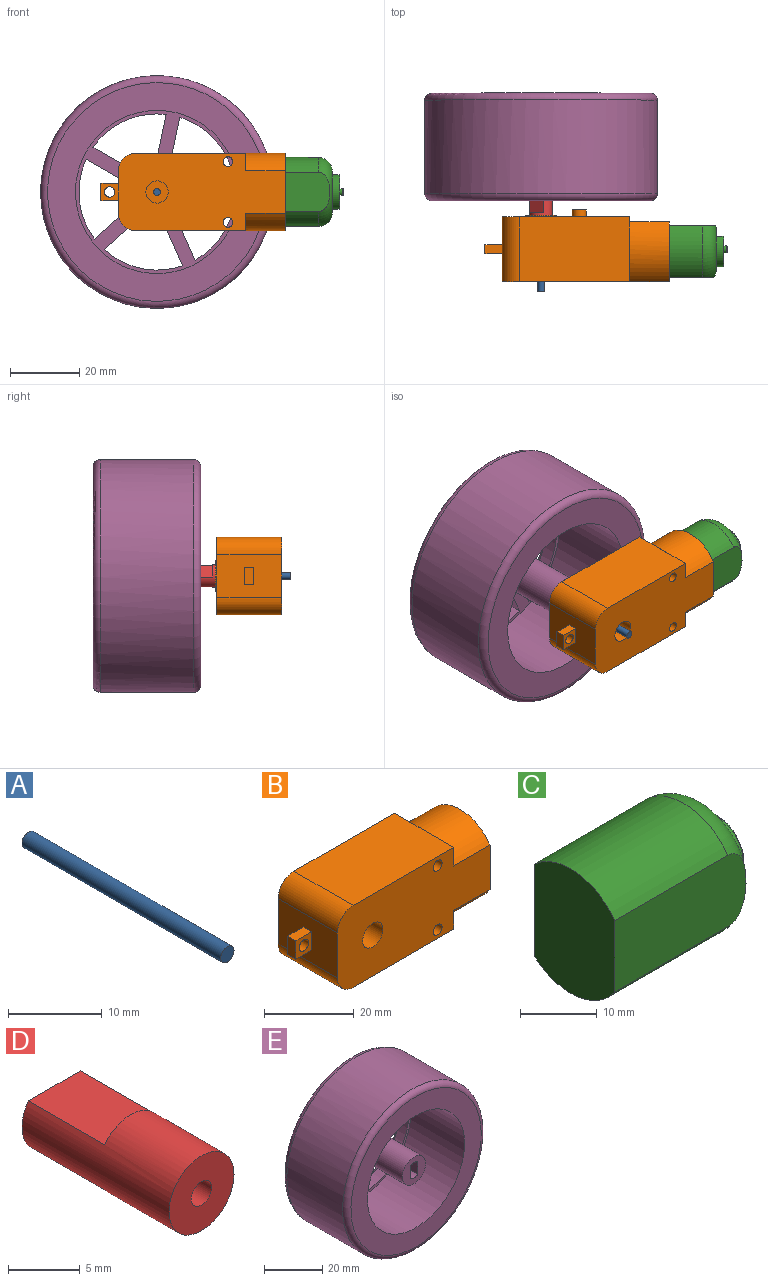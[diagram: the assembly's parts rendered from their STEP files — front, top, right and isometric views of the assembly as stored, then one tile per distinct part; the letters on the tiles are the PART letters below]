
ASSEMBLY  parts=5 mates=4
PART A: 3 faces, bbox 2x30x2 mm
  f0: cylinder r=1mm len=30mm, axis (0,1,0), area 188.5mm2, adj f1,f2
  f1: plane 2x2mm, normal (0,-1,0), area 3.1mm2, adj f0
  f2: plane 2x2mm, normal (0,1,0), area 3.1mm2, adj f0
PART B: 36 faces, bbox 53.1x20.7x22.3 mm
  f0: plane 36.7x22.3mm, normal (0,1,0), area 722mm2, adj f3,f5,f6,f7,f8,f9,f10,f12
  f1: cylinder r=3.2mm len=6.85mm, axis (0,1,0), area 137.7mm2, adj f33,f35
  f2: plane 9.35x5.08mm, normal (1,0,0), area 14mm2, adj f6,f13,f27
  f3: plane 22.3x9.35mm, normal (1,0,0), area 47.7mm2, adj f0,f6,f9,f25,f26,f27
  f4: plane 9.35x5.08mm, normal (1,0,0), area 14mm2, adj f9,f13,f25
  f5: plane 18.7x12.3mm, normal (-1,0,0), area 217mm2, adj f0,f7,f8,f13,f16,f17,f18,f19
  f6: plane 31.7x18.7mm, normal (0,0,1), area 592.8mm2, adj f0,f2,f3,f7,f13
  f7: cylinder r=5mm len=18.7mm, axis (0,1,0), area 146.9mm2, adj f0,f5,f6,f13
  f8: cylinder r=5mm len=18.7mm, axis (0,1,0), area 146.9mm2, adj f0,f5,f9,f13
  f9: plane 31.7x18.7mm, normal (0,0,-1), area 592.8mm2, adj f0,f3,f4,f8,f13
  f10: cylinder r=1.4mm len=18.7mm, axis (0,1,0), area 164.5mm2, adj f0,f13
  f11: cylinder r=3.2mm len=6.4mm, axis (0,1,0), area 127.7mm2, adj f13,f32
  f12: cylinder r=1.4mm len=18.7mm, axis (0,1,0), area 164.5mm2, adj f0,f13
  f13: plane 48.1x22.3mm, normal (0,-1,0), area 901.7mm2, adj f2,f4,f5,f6,f7,f8,f9,f10
  f14: cylinder r=2mm len=4mm, axis (0,-1,0), area 25.1mm2, adj f0,f15
  f15: plane 4x4mm, normal (0,1,0), area 12.6mm2, adj f14
  f16: plane 5x5mm, normal (0,-1,0), area 17.9mm2, adj f5,f17,f19,f20,f21
  f17: plane 5x2.6mm, normal (0,0,1), area 13mm2, adj f5,f16,f18,f20
  f18: plane 5x5mm, normal (0,1,0), area 17.9mm2, adj f5,f17,f19,f20,f21
  f19: plane 5x2.6mm, normal (0,0,-1), area 13mm2, adj f5,f16,f18,f20
  f20: plane 5x2.6mm, normal (-1,0,0), area 13mm2, adj f16,f17,f18,f19
  f21: cylinder r=1.5mm len=3mm, axis (0,-1,0), area 24.5mm2, adj f16,f18
  f22: cylinder r=9.95mm len=14.9mm, axis (-1,0,0), area 193.4mm2, adj f23,f28,f29,f30
  f23: plane 14.62x11.4mm, normal (0,-1,0), area 166.7mm2, adj f22,f24,f29,f30
  f24: cylinder r=9.95mm len=14.9mm, axis (-1,0,0), area 193.4mm2, adj f23,f28,f29,f30
  f25: cylinder r=11.15mm len=17.3mm, axis (-1,0,0), area 227.3mm2, adj f3,f4,f13,f26,f29
  f26: plane 15.64x11.4mm, normal (0,1,0), area 178.2mm2, adj f3,f25,f27,f29
  f27: cylinder r=11.15mm len=17.3mm, axis (-1,0,0), area 227.3mm2, adj f2,f3,f13,f26,f29
  f28: plane 11.42x11.4mm, normal (0,1,0), area 130.1mm2, adj f22,f24,f29,f30
  f29: plane 22.3x17.3mm, normal (1,0,0), area 76.6mm2, adj f13,f22,f23,f24,f25,f26,f27,f28
  f30: plane 19.9x14.9mm, normal (1,0,0), area 264.7mm2, adj f22,f23,f24,f28
  f31: cylinder r=1mm len=6mm, axis (0,1,0), area 37.7mm2, adj f32,f33
  f32: plane 6.4x6.4mm, normal (0,-1,0), area 29mm2, adj f11,f31
  f33: plane 6.4x6.4mm, normal (0,1,0), area 29mm2, adj f1,f31
  f34: cylinder r=4.4mm len=8.8mm, axis (0,-1,0), area 13.8mm2, adj f0,f35
  f35: plane 8.8x8.8mm, normal (0,1,0), area 28.7mm2, adj f1,f34
PART C: 14 faces, bbox 28.2x21.6x21.6 mm
  f0: plane 11.9x11.9mm, normal (1,0,0), area 38.3mm2, adj f6,f7,f8
  f1: plane 24.82x14.62mm, normal (0,1,0), area 353.1mm2, adj f2,f4,f5,f6
  f2: cylinder r=9.95mm len=20.9mm, axis (-1,0,0), area 354.6mm2, adj f1,f3,f5,f6
  f3: plane 24.24x11.42mm, normal (0,-1,0), area 269.2mm2, adj f2,f4,f5,f6
  f4: cylinder r=9.95mm len=20.9mm, axis (-1,0,0), area 354.6mm2, adj f1,f3,f5,f6
  f5: plane 19.9x14.9mm, normal (-1,0,0), area 264.7mm2, adj f1,f2,f3,f4
  f6: torus R=5.95mm, axis (-1,0,0), area 233.4mm2, adj f0,f1,f2,f3,f4
  f7: plane 6.7x2.29mm, normal (0,1,0), area 14.5mm2, adj f0,f8,f9,f13
  f8: cylinder r=5mm len=10mm, axis (-1,0,0), area 48.4mm2, adj f0,f7,f13
  f9: plane 9.6x8.55mm, normal (1,0,0), area 64.9mm2, adj f7,f10,f13
  f10: cylinder r=1mm len=2mm, axis (-1,0,0), area 5mm2, adj f9,f12
  f11: plane 1.6x1.6mm, normal (1,0,0), area 2mm2, adj f12
  f12: torus R=0.8mm, axis (1,0,0), area 1.8mm2, adj f10,f11
  f13: torus R=4.8mm, axis (1,0,0), area 7.6mm2, adj f7,f8,f9
PART D: 8 faces, bbox 6.4x14.5x6.4 mm
  f0: cylinder r=3.2mm len=14.5mm, axis (0,-1,0), area 202.5mm2, adj f2,f3,f4,f5,f6,f7
  f1: cylinder r=1mm len=14.5mm, axis (0,-1,0), area 91.1mm2, adj f2,f3
  f2: plane 6.4x3.84mm, normal (0,1,0), area 19.9mm2, adj f0,f1,f4,f6
  f3: plane 6.4x6.4mm, normal (0,-1,0), area 29mm2, adj f0,f1
  f4: plane 7.5x5.12mm, normal (0,0,-1), area 38.4mm2, adj f0,f2,f5
  f5: plane 5.12x1.28mm, normal (0,1,0), area 4.6mm2, adj f0,f4
  f6: plane 7.5x5.12mm, normal (0,0,1), area 38.4mm2, adj f0,f2,f7
  f7: plane 5.12x1.28mm, normal (0,1,0), area 4.6mm2, adj f0,f6
PART E: 53 faces, bbox 72.5x31x72.5 mm
  f0: plane 30x5.12mm, normal (-1,0,0), area 153.6mm2, adj f1,f3,f5,f27
  f1: cylinder r=3.2mm len=30mm, axis (0,1,0), area 123.6mm2, adj f0,f2,f5,f27
  f2: plane 30x5.12mm, normal (1,0,0), area 153.6mm2, adj f1,f3,f5,f27
  f3: cylinder r=3.2mm len=30mm, axis (0,1,0), area 123.6mm2, adj f0,f2,f5,f27
  f4: cylinder r=5.6mm len=25mm, axis (0,1,0), area 879.6mm2, adj f5,f28
  f5: plane 11.2x11.2mm, normal (0,-1,0), area 75.5mm2, adj f0,f1,f2,f3,f4
  f6: cylinder r=7.5mm len=4.26mm, axis (0,-1,0), area 21.5mm2, adj f7,f21,f28,f50
  f7: plane 15.18x4mm, normal (-1,0,0), area 60.7mm2, adj f6,f8,f28,f49
  f8: cylinder r=22.5mm len=18.7mm, axis (0,-1,0), area 97.1mm2, adj f7,f21,f28,f51
  f9: plane 12.28x8.92mm, normal (-0.81,0,0.59), area 60.7mm2, adj f10,f22,f28,f46
  f10: cylinder r=7.5mm len=5mm, axis (0,-1,0), area 21.5mm2, adj f9,f11,f28,f48
  f11: plane 14.44x4.69mm, normal (-0.31,0,-0.95), area 60.7mm2, adj f10,f22,f28,f47
  f12: plane 12.28x8.92mm, normal (-0.81,0,-0.59), area 60.7mm2, adj f13,f23,f28,f42
  f13: cylinder r=7.5mm len=5.26mm, axis (0,-1,0), area 21.5mm2, adj f12,f14,f28,f44
  f14: plane 12.28x8.92mm, normal (0.81,0,-0.59), area 60.7mm2, adj f13,f23,f28,f43
  f15: plane 14.44x4.69mm, normal (0.31,0,-0.95), area 60.7mm2, adj f16,f24,f28,f38
  f16: cylinder r=7.5mm len=5mm, axis (0,-1,0), area 21.5mm2, adj f15,f17,f28,f40
  f17: plane 12.28x8.92mm, normal (0.81,0,0.59), area 60.7mm2, adj f16,f24,f28,f39
  f18: plane 15.18x4mm, normal (1,0,0), area 60.7mm2, adj f19,f25,f28,f34
  f19: cylinder r=7.5mm len=4.26mm, axis (0,-1,0), area 21.5mm2, adj f18,f20,f28,f36
  f20: plane 14.44x4.69mm, normal (-0.31,0,0.95), area 60.7mm2, adj f19,f25,f28,f35
  f21: plane 14.44x4.69mm, normal (0.31,0,0.95), area 60.7mm2, adj f6,f8,f28,f52
  f22: cylinder r=22.5mm len=21.98mm, axis (0,-1,0), area 97.1mm2, adj f9,f11,f28,f45
  f23: cylinder r=22.5mm len=23.11mm, axis (0,-1,0), area 97.1mm2, adj f12,f14,f28,f41
  f24: cylinder r=22.5mm len=21.98mm, axis (0,-1,0), area 97.1mm2, adj f15,f17,f28,f37
  f25: cylinder r=22.5mm len=18.7mm, axis (0,-1,0), area 97.1mm2, adj f18,f20,f28,f33
  f26: cylinder r=33.5mm len=67mm, axis (0,-1,0), area 5683.1mm2, adj f31,f32
  f27: plane 63x63mm, normal (0,1,0), area 1662.2mm2, adj f0,f1,f2,f3,f32,f33,f34,f35
  f28: plane 47x47mm, normal (0,-1,0), area 523.9mm2, adj f4,f6,f7,f8,f9,f10,f11,f12
  f29: cylinder r=23.5mm len=47mm, axis (0,1,0), area 3839mm2, adj f28,f30
  f30: plane 63x63mm, normal (0,-1,0), area 1382.3mm2, adj f29,f31
  f31: torus R=31.5mm, axis (0,-1,0), area 646.9mm2, adj f26,f30
  f32: torus R=31.5mm, axis (0,1,0), area 646.9mm2, adj f26,f27
  f33: torus R=23.5mm, axis (0,1,0), area 40mm2, adj f25,f27,f34,f35
  f34: cylinder r=1mm len=17.06mm, axis (0,0,1), area 24.9mm2, adj f18,f27,f33,f36
  f35: cylinder r=1mm len=16.53mm, axis (-0.95,0,-0.31), area 24.9mm2, adj f20,f27,f33,f36
  f36: torus R=6.5mm, axis (0,1,0), area 8.9mm2, adj f19,f27,f34,f35
  f37: torus R=23.5mm, axis (0,1,0), area 40mm2, adj f24,f27,f38,f39
  f38: cylinder r=1mm len=16.53mm, axis (0.95,0,0.31), area 24.9mm2, adj f15,f27,f37,f40
  f39: cylinder r=1mm len=14.39mm, axis (-0.59,0,0.81), area 24.9mm2, adj f17,f27,f37,f40
  f40: torus R=6.5mm, axis (0,1,0), area 8.9mm2, adj f16,f27,f38,f39
  f41: torus R=23.5mm, axis (0,1,0), area 40mm2, adj f23,f27,f42,f43
  f42: cylinder r=1mm len=14.39mm, axis (0.59,0,-0.81), area 24.9mm2, adj f12,f27,f41,f44
  f43: cylinder r=1mm len=14.39mm, axis (0.59,0,0.81), area 24.9mm2, adj f14,f27,f41,f44
  f44: torus R=6.5mm, axis (0,1,0), area 8.9mm2, adj f13,f27,f42,f43
  f45: torus R=23.5mm, axis (0,1,0), area 40mm2, adj f22,f27,f46,f47
  f46: cylinder r=1mm len=14.39mm, axis (-0.59,0,-0.81), area 24.9mm2, adj f9,f27,f45,f48
  f47: cylinder r=1mm len=16.53mm, axis (0.95,0,-0.31), area 24.9mm2, adj f11,f27,f45,f48
  f48: torus R=6.5mm, axis (0,1,0), area 8.9mm2, adj f10,f27,f46,f47
  f49: cylinder r=1mm len=17.06mm, axis (0,0,-1), area 24.9mm2, adj f7,f27,f50,f51
  f50: torus R=6.5mm, axis (0,1,0), area 8.9mm2, adj f6,f27,f49,f52
  f51: torus R=23.5mm, axis (0,1,0), area 40mm2, adj f8,f27,f49,f52
  f52: cylinder r=1mm len=16.53mm, axis (-0.95,0,0.31), area 24.9mm2, adj f21,f27,f50,f51
PLACE A rot(axis=(0,-1,0),42.2deg) t=(-23.72,12.87,-1.64)mm
PLACE B t=(-21.85,9.87,-6.48)mm fixed
PLACE C t=(-21.85,9.87,-6.48)mm
PLACE D rot(axis=(0,-1,0),42.2deg) t=(-23.72,10.37,-1.64)mm
PLACE E rot(axis=(0,-1,0),132.2deg) t=(-29.05,49.87,-6.48)mm
MATE fastened A.f0 <-> E.f1  axis (0,1,0) through (-29.05,27.87,-6.48)mm
MATE fastened A.f0 <-> D.f0  axis (0,1,0) through (-29.05,27.87,-6.48)mm
MATE fastened B.f30 <-> C.f5  axis (1,0,0) through (-3.5,9.36,-6.48)mm
MATE revolute A.f0 <-> B.f1  axis (0,1,0) through (-29.05,12.87,-6.48)mm
